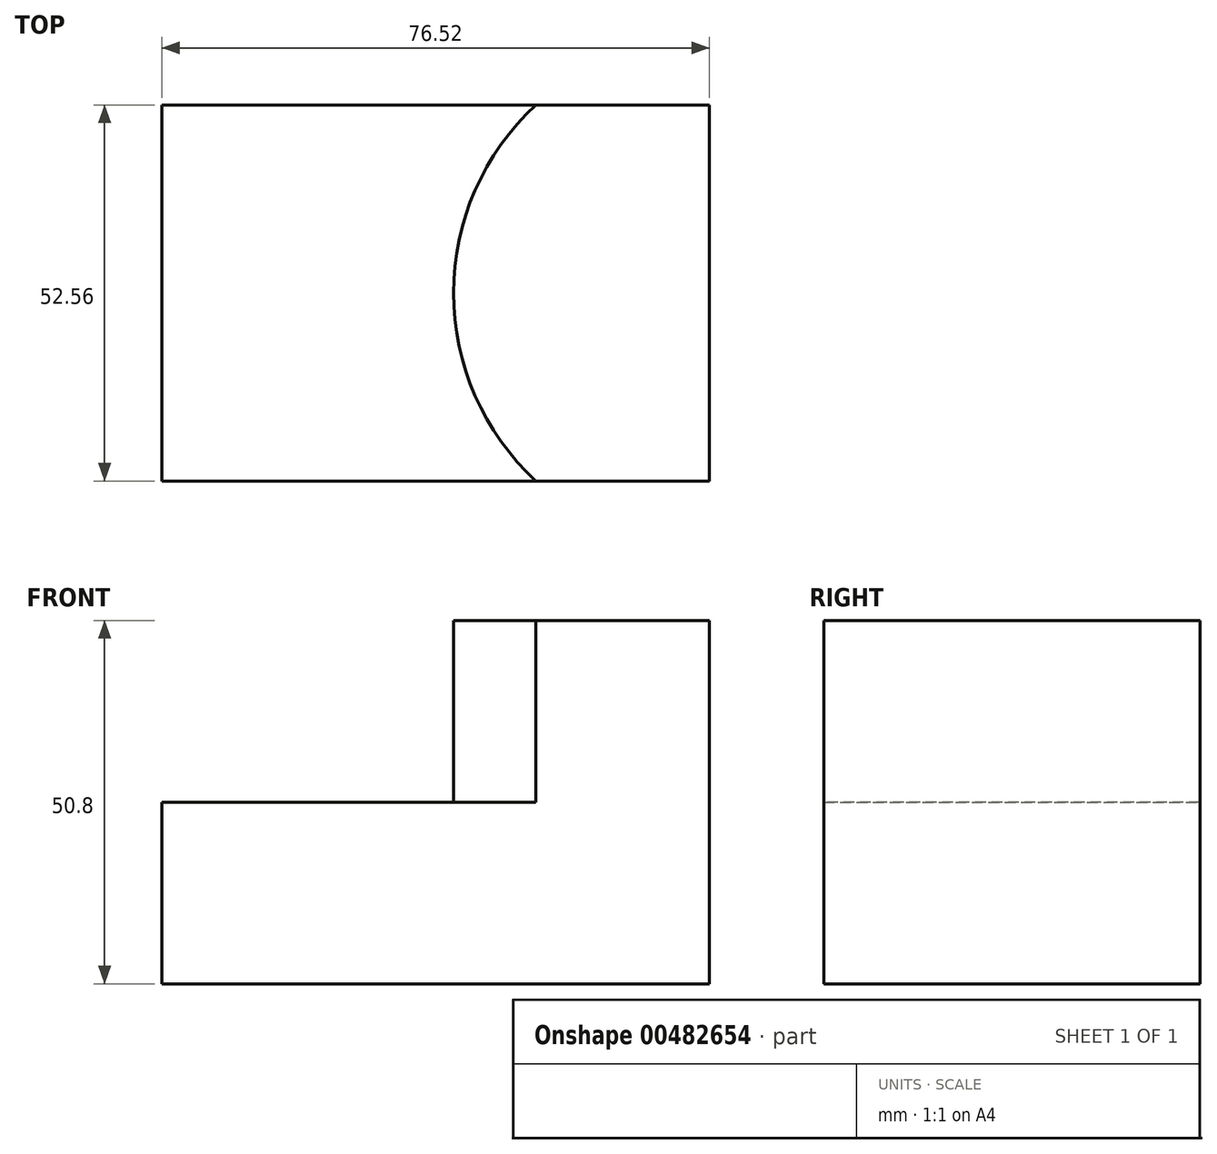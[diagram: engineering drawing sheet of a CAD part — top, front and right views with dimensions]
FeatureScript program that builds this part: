
annotation { "Feature Type Name" : "Feature", "Feature Type Description" : "" }
export const myFeature = defineFeature(function(context is Context, id is Id, definition is map)
    precondition{}
    {
        {
            var Q0;
            Q0=qCreatedBy(makeId("Top.planeOp"),FACE);
            var sketch = newSketch(context, id + "F0", { "sketchPlane" : qUnion([Q0])});
            skLineSegment(sketch, "E0.bottom", {"start": v(38.26, -26.28) * mm, "end": v(-38.26, -26.28) * mm});
            skLineSegment(sketch, "E0.top", {"start": v(38.26, 26.28) * mm, "end": v(-38.26, 26.28) * mm});
            skLineSegment(sketch, "E0.left", {"start": v(38.26, -26.28) * mm, "end": v(38.26, 26.28) * mm});
            skLineSegment(sketch, "E0.right", {"start": v(-38.26, -26.28) * mm, "end": v(-38.26, 26.28) * mm});
            skPoint(sketch, "E0.middle", {"position": v(0, 0) * mm});
            skSolve(sketch);
        }
        {
            var Q0;
            Q0 = qSketchRegion(id + "F0", true);
            extrude(context, id + "F1", {"entities" : qUnion([Q0]), "depth" : 25.4 * mm});
        }
        {
            var Q0;
            Q0=makeQuery(id+"F1.opExtrude","CAP_FACE",FACE,{"disambiguationData":[OSD([sQuery(id+"F0.wireOp",EDGE,"E0.bottom"),sQuery(id+"F0.wireOp",EDGE,"E0.top"),sQuery(id+"F0.wireOp",EDGE,"E0.left"),sQuery(id+"F0.wireOp",EDGE,"E0.right")])],"isStart":false});
            var sketch = newSketch(context, id + "F2", { "sketchPlane" : qUnion([Q0])});
            skCircle(sketch, "E1", {"center": v(38.26, 0) * mm, "radius": 35.74 * mm});
            skSolve(sketch);
        }
        {
            var Q0;
            {var subQ5=makeQuery(id+"F1.opExtrude","CAP_EDGE",EDGE,{"disambiguationData":[OSD([sQuery(id+"F0.wireOp",EDGE,"E0.left")])],"isStart":false});Q0=makeQuery(id+"F2.imprint","IMPRINT",FACE,{"disambiguationData":[TD([[makeQuery(id+"F2.imprint","IMPRINT",EDGE,{"derivedFrom":subQ5}),1.0]])]});}
            extrude(context, id + "F3", {"entities" : qUnion([Q0]), "operationType" : NewBodyOperationType.ADD, "depth" : 25.4 * mm});
        }
    });
